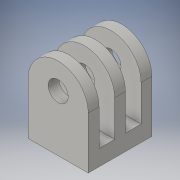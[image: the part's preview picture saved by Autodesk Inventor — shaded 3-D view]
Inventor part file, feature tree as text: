
AUTODESK INVENTOR PART (.ipt)
format: ipt  version: 2016 (Build 200138000, 138)  size: 155,136 bytes
history: native  units: in
note: dims shown in document units (in); Inventor stores cm internally (conversion verified against a paired STEP export)
features: extrude x3, sketch x3, fillet x1
ambient origin geometry x8: Origin, YZ Plane, XZ Plane, XY Plane, X Axis, Y Axis, Z Axis, Center Point
bodies: Solid1 (feature_tree)
feature tree (7):
  extrude  "Extrusion1"  Depth=0.2953in
  fillet  "Fillet1"  Radius=0.6496in
  extrude  "Extrusion8"  Depth=0.2559in
  extrude  "Extrusion9"  Depth=0.2953in
  sketch  "Sketch4"  dims[d0=0.2953in d1=0.2953in d2=0.6496in]
  sketch  "Sketch13"  dims[d3=0.1969in d4=0.2559in]
  sketch  "Sketch14"  dims[d5=0.626in d6=0.0in d7=0.2953in d47=0.1063in d48=0.1063in d49=0.1063in d50=0.626in d51=0.1535in d52=0.1535in d53=1.0in d54=0.0in d55=0.1575in d56=0.0in]
